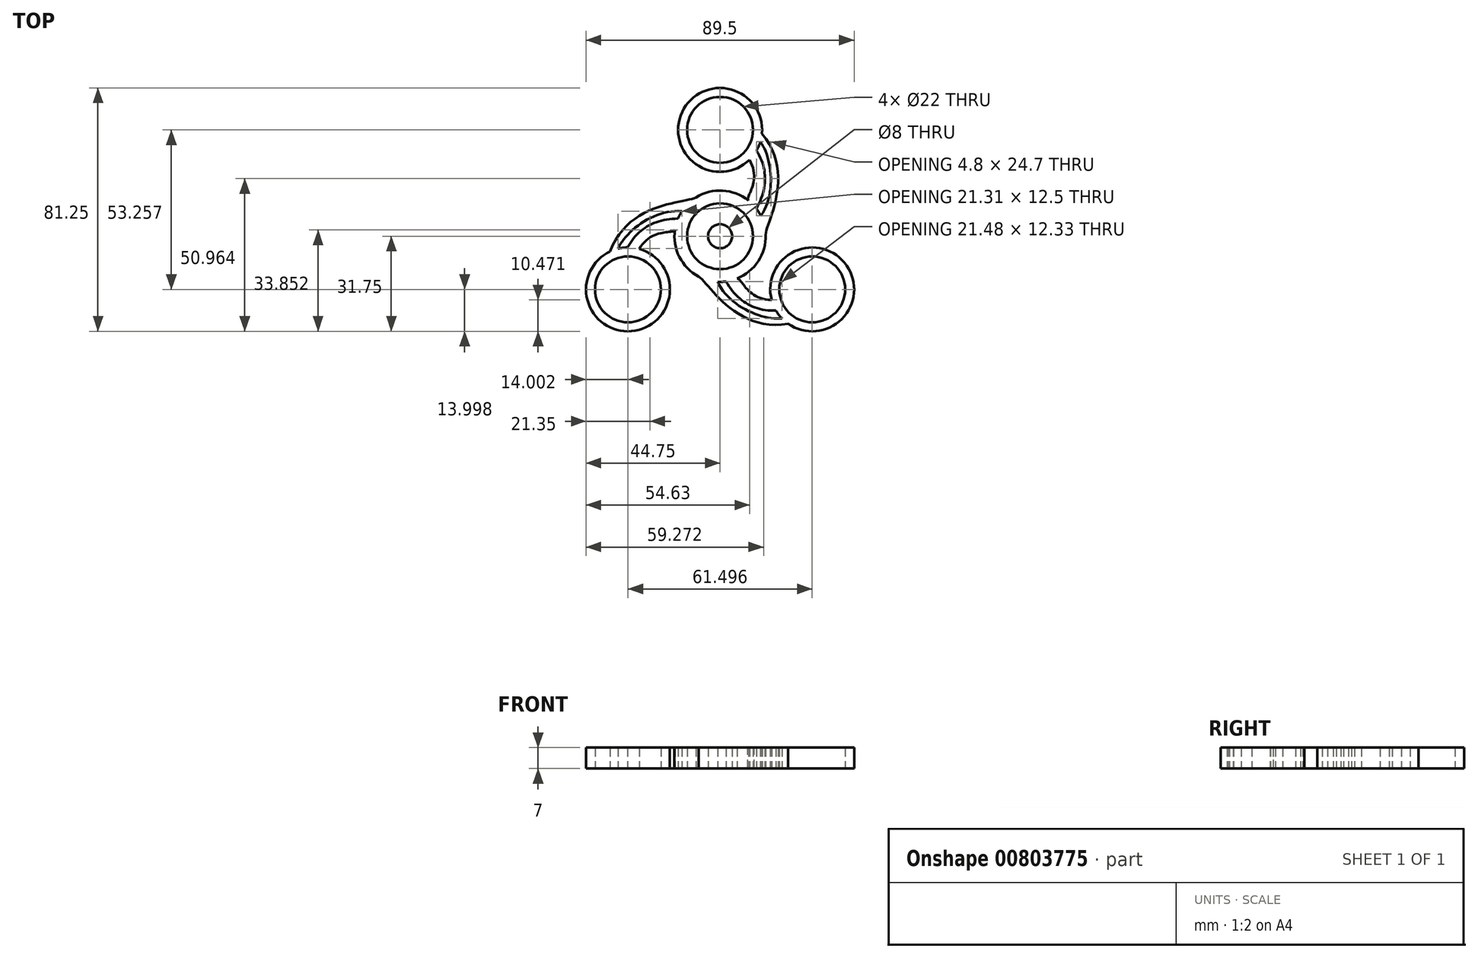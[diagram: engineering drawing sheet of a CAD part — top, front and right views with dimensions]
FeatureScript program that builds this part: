
annotation { "Feature Type Name" : "Feature", "Feature Type Description" : "" }
export const myFeature = defineFeature(function(context is Context, id is Id, definition is map)
    precondition{}
    {
        {
            var Q0;
            Q0=qCreatedBy(makeId("Top.planeOp"),FACE);
            var sketch = newSketch(context, id + "F0", { "sketchPlane" : qUnion([Q0])});
            skCircle(sketch, "E0", {"center": v(0, 0) * mm, "radius": 4 * mm});
            skCircle(sketch, "E1", {"center": v(0, 0) * mm, "radius": 11 * mm});
            skPoint(sketch, "E2.endSnap0", {"position": v(0, 5.5) * mm});
            skLineSegment(sketch, "E3", {"start": v(0, 48.5) * mm, "end": v(0, 46.5) * mm});
            skLineSegment(sketch, "E4", {"start": v(0, 46.5) * mm, "end": v(0, 35.5) * mm});
            skCircle(sketch, "E5", {"center": v(0, 35.5) * mm, "radius": 11 * mm});
            skLineSegment(sketch, "E6", {"start": v(0, 35.5) * mm, "end": v(0, 39.5) * mm});
            skCircle(sketch, "E7", {"center": v(0, 35.5) * mm, "radius": 4 * mm});
            skCircle(sketch, "E8", {"center": v(0, 0) * mm, "radius": 15.24 * mm});
            skLineSegment(sketch, "E9", {"start": v(0, 48.5) * mm, "end": v(0, 49.5) * mm});
            skCircle(sketch, "E10", {"center": v(0, 35.5) * mm, "radius": 14 * mm});
            skCircle(sketch, "E11.MirrorC", {"center": v(-30.75, -17.75) * mm, "radius": 11 * mm});
            skCircle(sketch, "E12.MirrorC", {"center": v(-30.75, -17.75) * mm, "radius": 4 * mm});
            skCircle(sketch, "E13.MirrorC", {"center": v(-30.75, -17.75) * mm, "radius": 14 * mm});
            skCircle(sketch, "E14.MirrorC", {"center": v(30.75, -17.75) * mm, "radius": 4 * mm});
            skCircle(sketch, "E15.MirrorC", {"center": v(30.75, -17.75) * mm, "radius": 11 * mm});
            skCircle(sketch, "E16.MirrorC", {"center": v(30.75, -17.75) * mm, "radius": 14 * mm});
            skFitSpline(sketch, "E17", {"points": [v(15.24, 0) * mm, v(13.95, 34.3) * mm], "startDerivative": vector(-1.52, 11.68) * mm, "endDerivative": vector(-35.23, 42.9) * mm});
            skFitSpline(sketch, "E18", {"points": [v(9.5, 11.9) * mm, v(9.81, 25.52) * mm], "startDerivative": vector(-4.45, 3.14) * mm, "endDerivative": vector(-12.75, 22.22) * mm});
            skFitSpline(sketch, "E19", {"points": [v(12.12, 9.23) * mm, v(12.17, 28.59) * mm], "startDerivative": vector(11.06, 19.55) * mm, "endDerivative": vector(-11.71, 18.36) * mm});
            skFitSpline(sketch, "E20", {"points": [v(13.43, 31.57) * mm, v(13.6, 6.86) * mm], "startDerivative": vector(11.14, -15.04) * mm, "endDerivative": vector(-16.06, -22.56) * mm});
            skFitSpline(sketch, "E21.MirrorCS", {"points": [v(5.56, -14.19) * mm, v(17.2, -21.26) * mm], "startDerivative": vector(4.94, 2.29) * mm, "endDerivative": vector(25.62, -0.07) * mm});
            skFitSpline(sketch, "E22.MirrorCS", {"points": [v(20.62, -27.42) * mm, v(-0.86, -15.21) * mm], "startDerivative": vector(-18.6, -2.13) * mm, "endDerivative": vector(-11.5, 25.2) * mm});
            skFitSpline(sketch, "E23.MirrorCS", {"points": [v(-7.62, -13.2) * mm, v(22.73, -29.23) * mm], "startDerivative": vector(10.87, -4.52) * mm, "endDerivative": vector(54.76, 9.06) * mm});
            skFitSpline(sketch, "E24.MirrorCS", {"points": [v(1.93, -15.12) * mm, v(18.67, -24.84) * mm], "startDerivative": vector(11.4, -19.35) * mm, "endDerivative": vector(21.76, 0.97) * mm});
            skFitSpline(sketch, "E25.MirrorCS", {"points": [v(-15.07, 2.28) * mm, v(-27, -4.26) * mm], "startDerivative": vector(-0.5, -5.42) * mm, "endDerivative": vector(-12.87, -22.16) * mm});
            skFitSpline(sketch, "E26.MirrorCS", {"points": [v(-14.06, 5.88) * mm, v(-30.84, -3.75) * mm], "startDerivative": vector(-22.46, -0.2) * mm, "endDerivative": vector(-10.04, -19.32) * mm});
            skFitSpline(sketch, "E27.MirrorCS", {"points": [v(-34.05, -4.15) * mm, v(-12.75, 8.35) * mm], "startDerivative": vector(7.46, 17.17) * mm, "endDerivative": vector(27.57, -2.63) * mm});
            skFitSpline(sketch, "E28.MirrorCS", {"points": [v(-7.62, 13.2) * mm, v(-36.68, -5.07) * mm], "startDerivative": vector(-9.35, -7.15) * mm, "endDerivative": vector(-19.53, -51.96) * mm});
            skSolve(sketch);
        }
        {
            var Q0;
            Q0=makeQuery(id+"F0.imprint","IMPRINT",FACE,{"disambiguationData":[TD([[makeQuery(id+"F0.imprint","IMPRINT",EDGE,{"derivedFrom":sQuery(id+"F0.wireOp",EDGE,"E0")}),-1.0]])]});
            extrude(context, id + "F1", {"entities" : qUnion([Q0]), "depth" : 7 * mm, "offsetDistance" : 25 * mm});
        }
        {
            var Q0;
            Q0=qSketchRegion(id+"F0",true);
            extrude(context, id + "F2", {"entities" : qUnion([Q0]), "depth" : 7 * mm, "offsetDistance" : 25 * mm});
        }
    });
